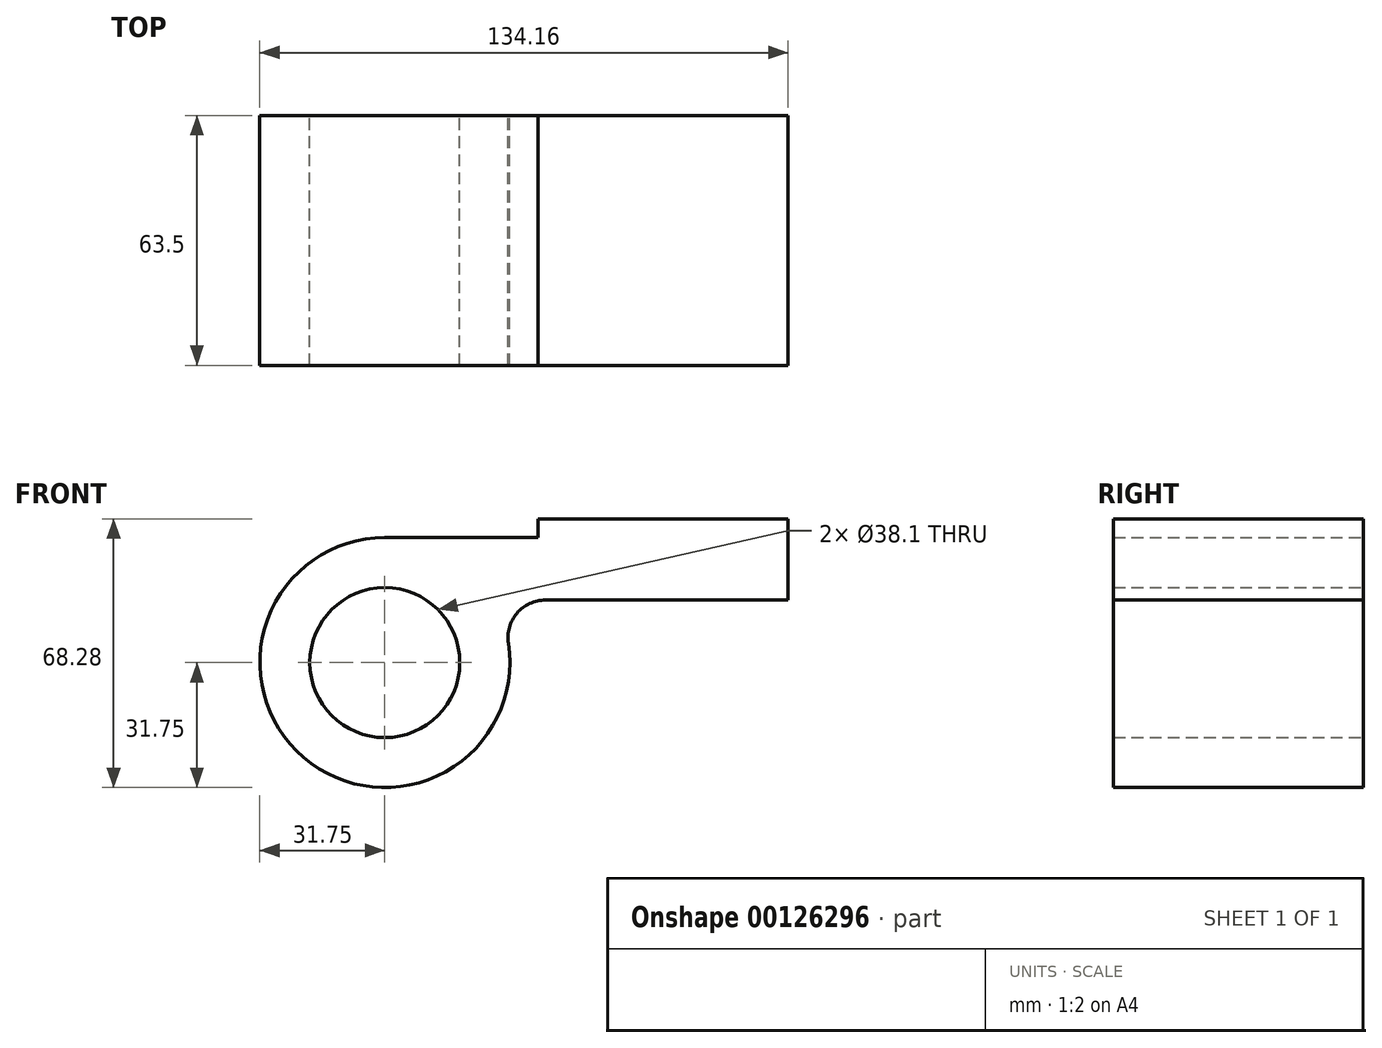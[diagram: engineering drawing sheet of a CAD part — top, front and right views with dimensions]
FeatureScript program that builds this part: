
annotation { "Feature Type Name" : "Feature", "Feature Type Description" : "" }
export const myFeature = defineFeature(function(context is Context, id is Id, definition is map)
    precondition{}
    {
        {
            var Q0;
            Q0=qCreatedBy(makeId("Front.planeOp"),FACE);
            var sketch = newSketch(context, id + "F0", { "sketchPlane" : qUnion([Q0])});
            skCircle(sketch, "E0", {"center": v(0, 0) * mm, "radius": 19.05 * mm});
            skLineSegment(sketch, "E1", {"start": v(0, 31.75) * mm, "end": v(38.89, 31.75) * mm});
            skLineSegment(sketch, "E2", {"start": v(38.89, 31.75) * mm, "end": v(38.89, 36.53) * mm});
            skLineSegment(sketch, "E3", {"start": v(38.89, 36.53) * mm, "end": v(102.41, 36.53) * mm});
            skLineSegment(sketch, "E4", {"start": v(102.41, 36.53) * mm, "end": v(102.41, 15.88) * mm});
            skArc(sketch, "E5", {"start": v(0, 31.75) * mm, "mid": v(-20.65, -24.12) * mm, "end": v(31.37, 4.88) * mm});
            skLineSegment(sketch, "E6", {"start": v(102.41, 15.87) * mm, "end": v(40.78, 15.87) * mm});
            skArc(sketch, "E7", {"start": v(40.78, 15.87) * mm, "mid": v(33.55, 12.55) * mm, "end": v(31.37, 4.88) * mm});
            skLineSegment(sketch, "E8", {"start": v(84.15, 36.53) * mm, "end": v(84.15, 15.88) * mm, "construction": true});
            skLineSegment(sketch, "E9", {"start": v(50.8, 36.53) * mm, "end": v(50.8, 15.88) * mm, "construction": true});
            skLineSegment(sketch, "E10", {"start": v(45.24, 36.53) * mm, "end": v(45.24, 15.88) * mm, "construction": true});
            skLineSegment(sketch, "E11", {"start": v(56.36, 36.53) * mm, "end": v(56.36, 15.88) * mm, "construction": true});
            skLineSegment(sketch, "E12", {"start": v(78.59, 36.53) * mm, "end": v(78.59, 15.88) * mm, "construction": true});
            skLineSegment(sketch, "E13", {"start": v(89.71, 36.53) * mm, "end": v(89.71, 15.88) * mm, "construction": true});
            skLineSegment(sketch, "E14", {"start": v(13.68, -28.65) * mm, "end": v(71.6, 15.87) * mm, "construction": true});
            skSolve(sketch);
        }
        {
            var Q0;
            Q0 = qSketchRegion(id + "F0", true);
            extrude(context, id + "F1", {"entities" : qUnion([Q0]), "depth" : 63.5 * mm});
        }
    });
